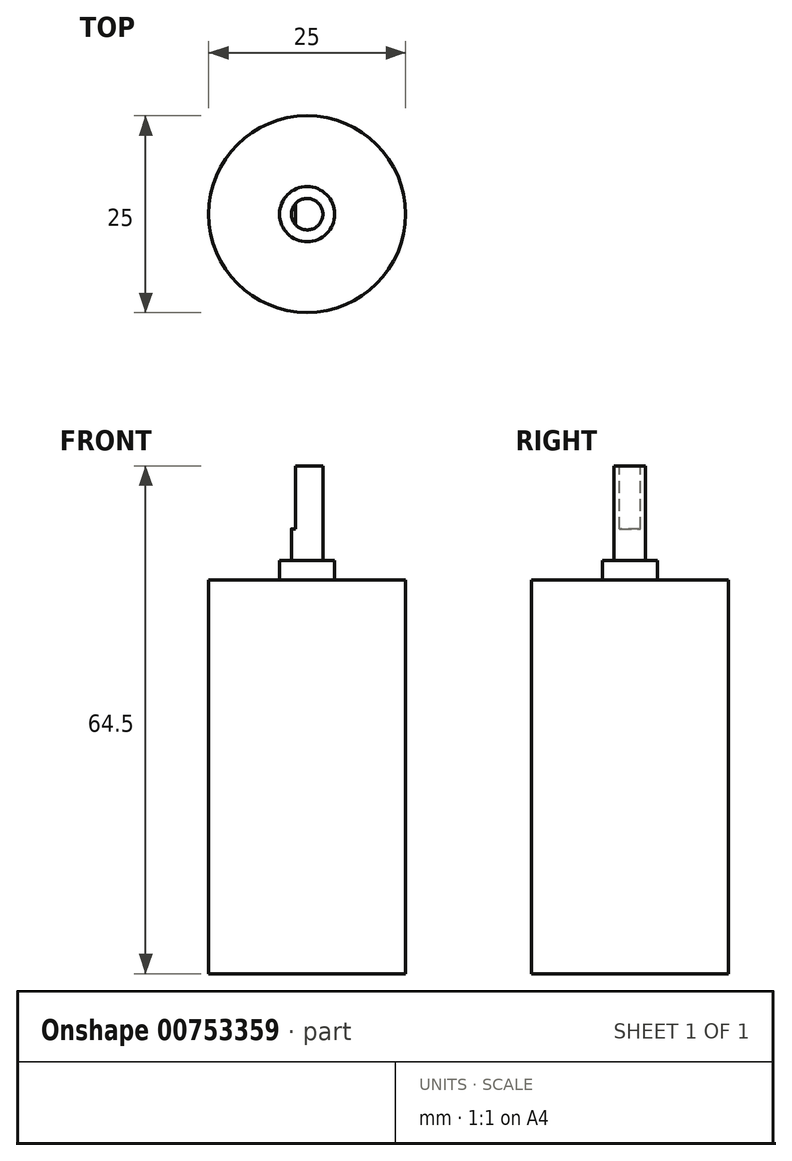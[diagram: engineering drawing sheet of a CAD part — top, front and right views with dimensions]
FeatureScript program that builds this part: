
annotation { "Feature Type Name" : "Feature", "Feature Type Description" : "" }
export const myFeature = defineFeature(function(context is Context, id is Id, definition is map)
    precondition{}
    {
        {
            var Q0;
            Q0=qCreatedBy(makeId("Right.planeOp"),FACE);
            var sketch = newSketch(context, id + "F0", { "sketchPlane" : qUnion([Q0])});
            skLineSegment(sketch, "E0", {"start": v(0, -25.54) * mm, "end": v(-12.5, -25.54) * mm});
            skLineSegment(sketch, "E1", {"start": v(-12.5, -25.54) * mm, "end": v(-12.5, 24.46) * mm});
            skLineSegment(sketch, "E2", {"start": v(-12.5, 24.46) * mm, "end": v(-3.5, 24.46) * mm});
            skLineSegment(sketch, "E3", {"start": v(-3.5, 24.46) * mm, "end": v(-3.5, 26.96) * mm});
            skLineSegment(sketch, "E4", {"start": v(-3.5, 26.96) * mm, "end": v(-2, 26.96) * mm});
            skLineSegment(sketch, "E5", {"start": v(-2, 26.96) * mm, "end": v(-2, 38.96) * mm});
            skLineSegment(sketch, "E6", {"start": v(-2, 38.96) * mm, "end": v(0, 38.96) * mm});
            skLineSegment(sketch, "E7", {"start": v(0, 38.96) * mm, "end": v(0, -25.54) * mm});
            skSolve(sketch);
        }
        {
            var Q0;
            Q0 = qSketchRegion(id + "F0", true);
            var Q1;
            Q1=sQuery(id+"F0.wireOp",EDGE,"E7");
            revolve(context, id + "F1", {"surfaceOperationType" : NewSurfaceOperationType.NEW, "entities" : qUnion([Q0]), "axis" : qUnion([Q1]), "revolveType" : RevolveType.FULL});
        }
        {
            var Q0;
            Q0=makeQuery(id+"F1.opRevolve","SWEPT_FACE",FACE,{"disambiguationData":[OSD([sQuery(id+"F0.wireOp",EDGE,"E6")])]});
            var sketch = newSketch(context, id + "F2", { "sketchPlane" : qUnion([Q0])});
            skCircle(sketch, "E8", {"center": v(0, 0) * mm, "radius": 2 * mm});
            skLineSegment(sketch, "E9", {"start": v(-1.5, -1.32) * mm, "end": v(-1.5, 1.32) * mm});
            skSolve(sketch);
        }
        {
            var Q0;
            {var subQ0=sQuery(id+"F2.wireOp",EDGE,"E9");Q0=makeQuery(id+"F2.imprint","IMPRINT",FACE,{"disambiguationData":[TD([[makeQuery(id+"F2.imprint","IMPRINT",EDGE,{"derivedFrom":subQ0}),1.0]])]});}
            extrude(context, id + "F3", {"entities" : qUnion([Q0]), "operationType" : NewBodyOperationType.REMOVE, "oppositeDirection" : true, "depth" : 8 * mm, "offsetDistance" : 25 * mm});
        }
    });
